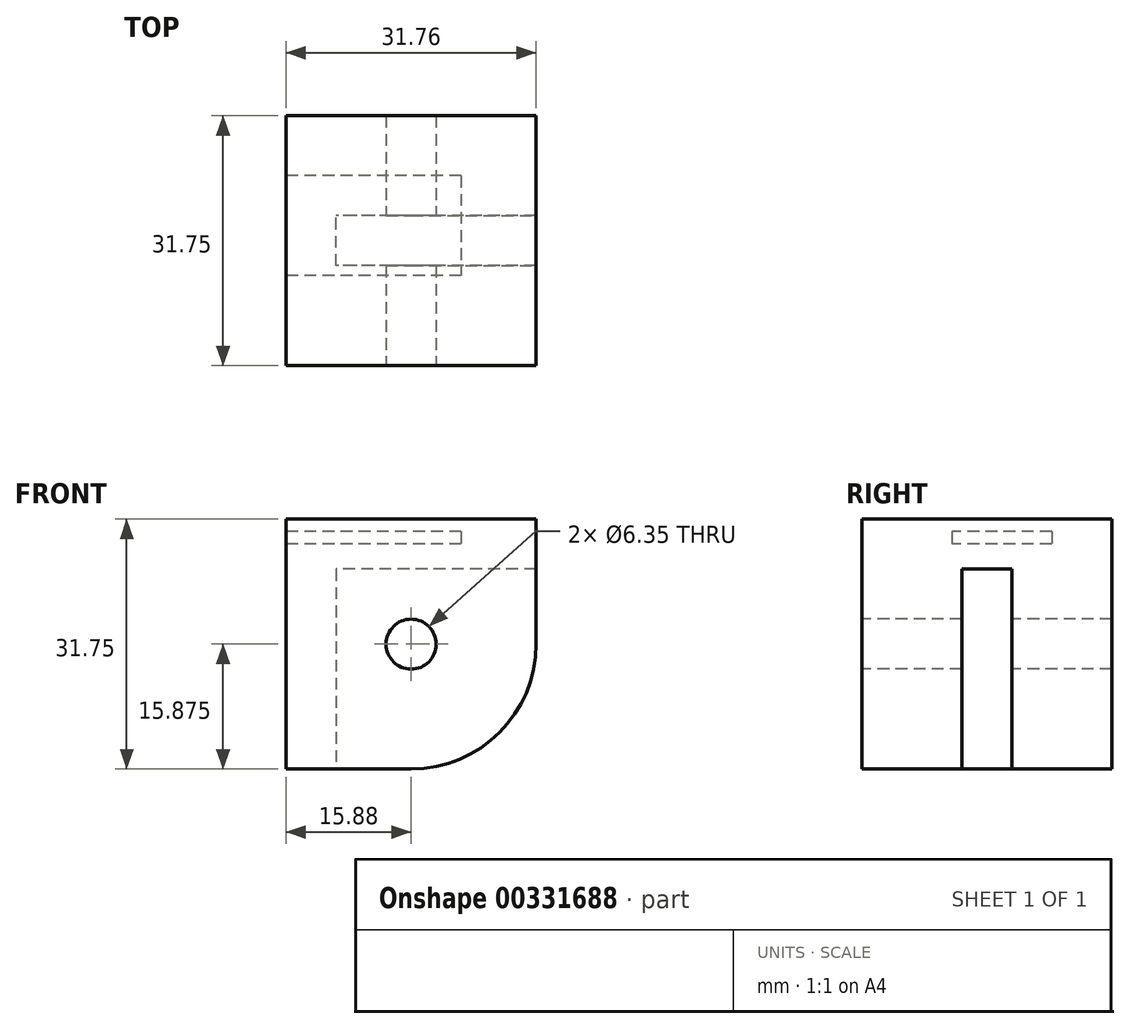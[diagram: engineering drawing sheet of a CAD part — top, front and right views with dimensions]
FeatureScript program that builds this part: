
annotation { "Feature Type Name" : "Feature", "Feature Type Description" : "" }
export const myFeature = defineFeature(function(context is Context, id is Id, definition is map)
    precondition{}
    {
        {
            var Q0;
            Q0=qCreatedBy(makeId("Front.planeOp"),FACE);
            var sketch = newSketch(context, id + "F0", { "sketchPlane" : qUnion([Q0])});
            skLineSegment(sketch, "E0", {"start": v(15.87, 0) * mm, "end": v(-15.88, 0) * mm});
            skLineSegment(sketch, "E1", {"start": v(-15.88, 0) * mm, "end": v(-15.87, -31.75) * mm});
            skLineSegment(sketch, "E2", {"start": v(-15.88, -31.75) * mm, "end": v(0, -31.75) * mm});
            skLineSegment(sketch, "E3", {"start": v(15.87, 0) * mm, "end": v(15.87, -15.88) * mm});
            skArc(sketch, "E4", {"start": v(0, -31.75) * mm, "mid": v(11.23, -27.1) * mm, "end": v(15.87, -15.88) * mm});
            skLineSegment(sketch, "E5.bottom", {"start": v(0, -15.88) * mm, "end": v(0, -15.88) * mm});
            skLineSegment(sketch, "E5.top", {"start": v(0, -15.88) * mm, "end": v(0, -15.88) * mm});
            skLineSegment(sketch, "E5.left", {"start": v(0, -15.88) * mm, "end": v(0, -15.88) * mm});
            skLineSegment(sketch, "E5.right", {"start": v(0, -15.88) * mm, "end": v(0, -15.88) * mm});
            skCircle(sketch, "E6", {"center": v(0, -15.88) * mm, "radius": 3.18 * mm});
            skSolve(sketch);
        }
        {
            var Q0;
            Q0=qSketchRegion(id+"F0",true);
            extrude(context, id + "F1", {"entities" : qUnion([Q0]), "oppositeDirection" : true, "depth" : 31.75 * mm});
        }
        {
            var Q0;
            Q0=makeQuery(id+"F1.opExtrude","SWEPT_FACE",FACE,{"disambiguationData":[OSD([sQuery(id+"F0.wireOp",EDGE,"E1")])]});
            var sketch = newSketch(context, id + "F2", { "sketchPlane" : qUnion([Q0])});
            skLineSegment(sketch, "E7.bottom", {"start": v(-24.13, -1.59) * mm, "end": v(-11.43, -1.59) * mm});
            skLineSegment(sketch, "E7.top", {"start": v(-24.13, -3.17) * mm, "end": v(-11.43, -3.17) * mm});
            skLineSegment(sketch, "E7.left", {"start": v(-24.13, -1.59) * mm, "end": v(-24.13, -3.17) * mm});
            skLineSegment(sketch, "E7.right", {"start": v(-11.43, -1.59) * mm, "end": v(-11.43, -3.17) * mm});
            skSolve(sketch);
        }
        {
            var Q0;
            Q0=qSketchRegion(id+"F2",true);
            extrude(context, id + "F3", {"entities" : qUnion([Q0]), "operationType" : NewBodyOperationType.REMOVE, "oppositeDirection" : true, "depth" : 22.22 * mm});
        }
        {
            var Q0;
            Q0=makeQuery(id+"F1.opExtrude","SWEPT_FACE",FACE,{"disambiguationData":[OSD([sQuery(id+"F0.wireOp",EDGE,"E2")])]});
            var sketch = newSketch(context, id + "F4", { "sketchPlane" : qUnion([Q0])});
            skLineSegment(sketch, "E8.bottom", {"start": v(15.88, -12.7) * mm, "end": v(-9.52, -12.7) * mm});
            skLineSegment(sketch, "E8.top", {"start": v(15.88, -19.05) * mm, "end": v(-9.52, -19.05) * mm});
            skLineSegment(sketch, "E8.left", {"start": v(15.88, -12.7) * mm, "end": v(15.88, -19.05) * mm});
            skLineSegment(sketch, "E8.right", {"start": v(-9.52, -12.7) * mm, "end": v(-9.52, -19.05) * mm});
            skSolve(sketch);
        }
        {
            var Q0;
            {var subQ0=sQuery(id+"F4.wireOp",EDGE,"E8.left");Q0=makeQuery(id+"F4.imprint","IMPRINT",FACE,{"disambiguationData":[TD([[makeQuery(id+"F4.imprint","IMPRINT",EDGE,{"derivedFrom":subQ0}),-1.0]])]});}
            var Q1;
            {var subQ0=sQuery(id+"F4.wireOp",EDGE,"E8.right");Q1=makeQuery(id+"F4.imprint","IMPRINT",FACE,{"disambiguationData":[TD([[makeQuery(id+"F4.imprint","IMPRINT",EDGE,{"derivedFrom":subQ0}),1.0]])]});}
            extrude(context, id + "F5", {"entities" : qUnion([Q0, Q1]), "operationType" : NewBodyOperationType.REMOVE, "oppositeDirection" : true, "depth" : 25.4 * mm});
        }
    });
